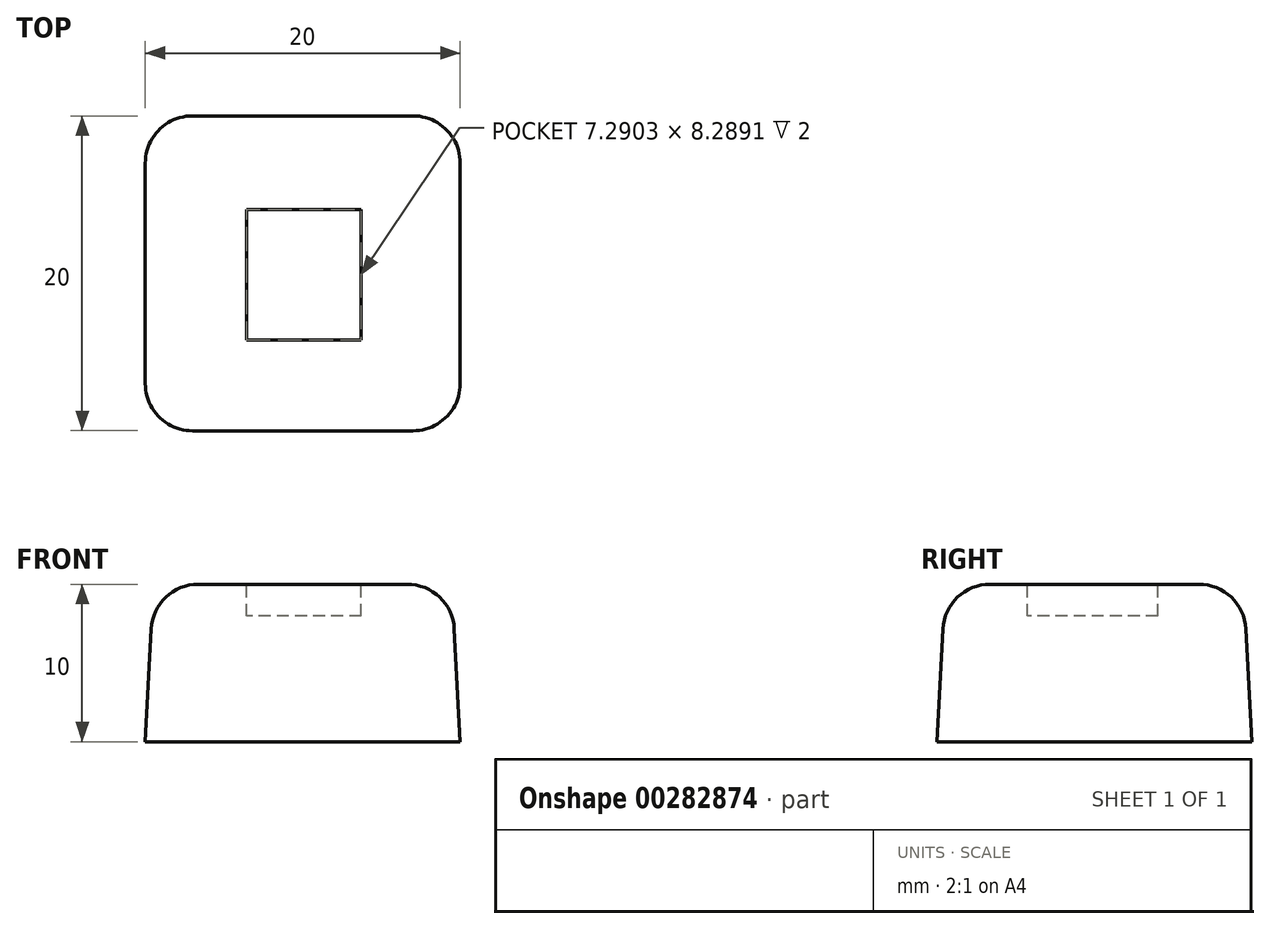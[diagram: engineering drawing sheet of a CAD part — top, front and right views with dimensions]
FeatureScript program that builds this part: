
annotation { "Feature Type Name" : "Feature", "Feature Type Description" : "" }
export const myFeature = defineFeature(function(context is Context, id is Id, definition is map)
    precondition{}
    {
        {
            var Q0;
            Q0=qCreatedBy(makeId("Top.planeOp"),FACE);
            var sketch = newSketch(context, id + "F0", { "sketchPlane" : qUnion([Q0])});
            skLineSegment(sketch, "E0.bottom", {"start": v(10, 9.13) * mm, "end": v(-10, 9.13) * mm});
            skLineSegment(sketch, "E0.top", {"start": v(10, -10.87) * mm, "end": v(-10, -10.87) * mm});
            skLineSegment(sketch, "E0.left", {"start": v(10, 9.13) * mm, "end": v(10, -10.87) * mm});
            skLineSegment(sketch, "E0.right", {"start": v(-10, 9.13) * mm, "end": v(-10, -10.87) * mm});
            skPoint(sketch, "E0.middle", {"position": v(0, -0.87) * mm});
            skSolve(sketch);
        }
        {
            var Q0;
            Q0 = qSketchRegion(id + "F0", true);
            extrude(context, id + "F1", {"entities" : qUnion([Q0]), "depth" : 10 * mm, "hasDraft" : true, "draftAngle" : 3 * degree, "draftPullDirection" : true});
        }
        {
            var Q0;
            Q0=makeQuery(id+"F1.opExtrude","CAP_EDGE",EDGE,{"disambiguationData":[OSD([sQuery(id+"F0.wireOp",EDGE,"E0.bottom")])],"isStart":false});
            var Q1;
            Q1=makeQuery(id+"F1.opExtrude","SWEPT_EDGE",EDGE,{"disambiguationData":[OSD([sQuery(id+"F0.wireOp",EDGE,"E0.bottom"),sQuery(id+"F0.wireOp",EDGE,"E0.right")])]});
            var Q2;
            Q2=makeQuery(id+"F1.opExtrude","CAP_EDGE",EDGE,{"disambiguationData":[OSD([sQuery(id+"F0.wireOp",EDGE,"E0.right")])],"isStart":false});
            var Q3;
            Q3=makeQuery(id+"F1.opExtrude","SWEPT_EDGE",EDGE,{"disambiguationData":[OSD([sQuery(id+"F0.wireOp",EDGE,"E0.top"),sQuery(id+"F0.wireOp",EDGE,"E0.right")])]});
            var Q4;
            Q4=makeQuery(id+"F1.opExtrude","CAP_EDGE",EDGE,{"disambiguationData":[OSD([sQuery(id+"F0.wireOp",EDGE,"E0.top")])],"isStart":false});
            var Q5;
            Q5=makeQuery(id+"F1.opExtrude","CAP_EDGE",EDGE,{"disambiguationData":[OSD([sQuery(id+"F0.wireOp",EDGE,"E0.left")])],"isStart":false});
            var Q6;
            Q6=makeQuery(id+"F1.opExtrude","SWEPT_EDGE",EDGE,{"disambiguationData":[OSD([sQuery(id+"F0.wireOp",EDGE,"E0.bottom"),sQuery(id+"F0.wireOp",EDGE,"E0.left")])]});
            var Q7;
            Q7=makeQuery(id+"F1.opExtrude","SWEPT_EDGE",EDGE,{"disambiguationData":[OSD([sQuery(id+"F0.wireOp",EDGE,"E0.top"),sQuery(id+"F0.wireOp",EDGE,"E0.left")])]});
            fillet(context, id + "F2", {"entities" : qUnion([Q0, Q1, Q2, Q3, Q4, Q5, Q6, Q7]), "radius" : 3 * mm, "tangentPropagation" : true, "allowEdgeOverflow" : false});
        }
        {
            var Q0;
            Q0=makeQuery(id+"F1.opExtrude","CAP_FACE",FACE,{"disambiguationData":[OSD([sQuery(id+"F0.wireOp",EDGE,"E0.bottom"),sQuery(id+"F0.wireOp",EDGE,"E0.top"),sQuery(id+"F0.wireOp",EDGE,"E0.left"),sQuery(id+"F0.wireOp",EDGE,"E0.right")])],"isStart":false});
            var sketch = newSketch(context, id + "F3", { "sketchPlane" : qUnion([Q0])});
            skPoint(sketch, "E1.middle", {"position": v(0, 0) * mm});
            skLineSegment(sketch, "E2", {"start": v(-3.58, 3.17) * mm, "end": v(-3.58, -5.12) * mm});
            skLineSegment(sketch, "E3", {"start": v(-3.58, -5.12) * mm, "end": v(3.7, -5.12) * mm});
            skLineSegment(sketch, "E4", {"start": v(3.7, -5.12) * mm, "end": v(3.7, 3.17) * mm});
            skLineSegment(sketch, "E5", {"start": v(3.7, 3.17) * mm, "end": v(-3.58, 3.17) * mm});
            skSolve(sketch);
        }
        {
            var Q0;
            Q0=makeQuery(id+"F3.imprint","IMPRINT",FACE,{"disambiguationData":[TD([[makeQuery(id+"F3.imprint","IMPRINT",EDGE,{"derivedFrom":sQuery(id+"F3.wireOp",EDGE,"E2")}),1.0]])]});
            extrude(context, id + "F4", {"entities" : qUnion([Q0]), "operationType" : NewBodyOperationType.REMOVE, "oppositeDirection" : true, "depth" : 2 * mm});
        }
    });
